# Revit family: 67L-W-Dome
name_source: partatom
category: Lighting Fixtures
units: mm (PartAtom-declared; Revit-internal decimal feet)

## family parameters
Always vertical = Yes
Cut with Voids When Loaded = No
Host = Wall
Light Source = Yes
OmniClass Number = 23.80.70.11.14.17
OmniClass Title = Direct/Indirect
Part Type = Normal
Room Calculation Point = No
Round Connector Dimension = Use Diameter
Shared = Yes

## types (6) — shared parameters
Apparent Load = 5 VA
Assembly Code = D5020210
Color Filter = 16777215
Description = The NOTE 67L Wall Mount brings direct illumination, ADA compliance, performance and versatility, all within a slim profile and a fresh, contemporary style
Dimming Lamp Color Temperature Shift = <None>
Emit Shape Visible in Rendering = No
Emit from Rectangle Length = 3 "
Emit from Rectangle Width = 47 "
Glass = White Glass
Lamp = LED
Load Classification = Lighting
Manufacturer = Litecontrol
Model = 67L-W-Dome
Photometric Notes = Photometric Web files Download in below link
Photometric Web File = 67L-W-D-4-4-DM-C1-35K-D055.IES
Power Factor = 1
Tilt Angle = 0.00°
Type Comments = Lighting Fixture
URL = https://www.currentlighting.com
Voltage = 120 V
Wattage Comments = 550 to 1800 lumens/ft
Watts = 5 W
Width = 48 "
zero-valued in all types: Default Elevation

## per-type parameters (varying)
| type | Housing Material |
| Note 67L-Carbon Black | Paint - Carbon Black |
| Note 67L-Textured Matte White | Paint -  Textured Matte White |
| Note 67L-Light Silver | Paint -  Light Silver |
| Note 67L-Machined Aluminum | Paint - Machined Aluminum |
| Note 67L-Textured Camera Black | Paint - Textured Camera Black |
| Note 67L-Matte White | Paint -  Matte White |

## geometry (parser evidence)
native form markers: Sweep x5
no freeform markers — native parametric forms only
